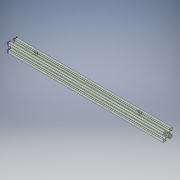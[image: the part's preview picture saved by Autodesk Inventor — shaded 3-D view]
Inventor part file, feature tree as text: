
AUTODESK INVENTOR PART (.ipt)
format: ipt  version: 2017 (Build 210142000, 142)  size: 387,584 bytes
history: native  units: in
note: dims shown in document units (in); Inventor stores cm internally (conversion verified against a paired STEP export)
features: sketch x1
ambient origin geometry x8: Origin, YZ Plane, XZ Plane, XY Plane, X Axis, Y Axis, Z Axis, Center Point
bodies: Solid1 (feature_tree)
feature tree (1):
  sketch  "Sketch2"
